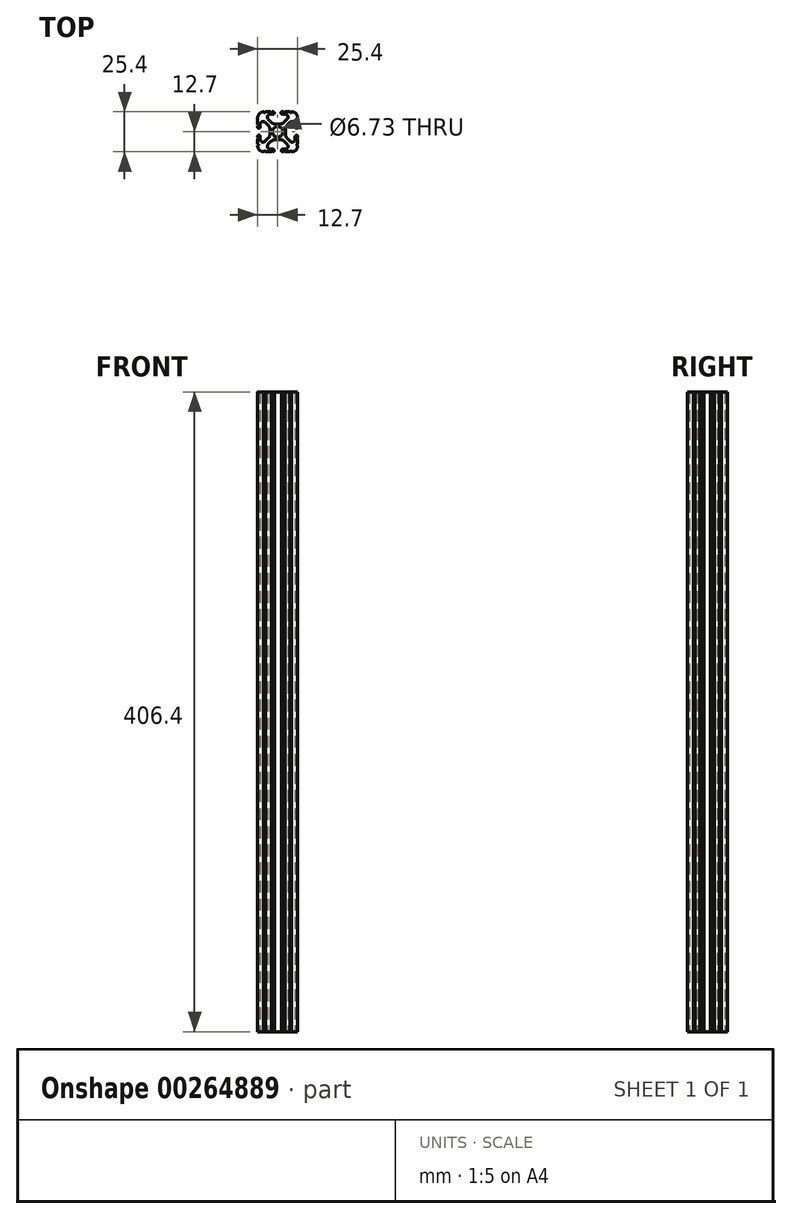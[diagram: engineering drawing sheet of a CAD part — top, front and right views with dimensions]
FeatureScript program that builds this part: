
annotation { "Feature Type Name" : "Feature", "Feature Type Description" : "" }
export const myFeature = defineFeature(function(context is Context, id is Id, definition is map)
    precondition{}
    {
        {
            var Q0;
            Q0=qCreatedBy(makeId("Top.planeOp"),FACE);
            var sketch = newSketch(context, id + "F0", { "sketchPlane" : qUnion([Q0])});
            skCircle(sketch, "E0", {"center": v(-12.7, 12.7) * mm, "radius": 3.36 * mm});
            skLineSegment(sketch, "E1.bottom", {"start": v(-11.24, 17.64) * mm, "end": v(-14.16, 17.64) * mm});
            skLineSegment(sketch, "E1.top", {"start": v(-11.24, 7.76) * mm, "end": v(-14.16, 7.76) * mm});
            skLineSegment(sketch, "E1.left", {"start": v(-7.76, 14.16) * mm, "end": v(-7.76, 11.24) * mm});
            skLineSegment(sketch, "E1.right", {"start": v(-17.64, 14.16) * mm, "end": v(-17.64, 11.24) * mm});
            skPoint(sketch, "E2.visualSharp", {"position": v(-25.4, 25.4) * mm});
            skPoint(sketch, "E3.visualSharp", {"position": v(0, 25.4) * mm});
            skPoint(sketch, "E4.visualSharp", {"position": v(0, 0) * mm});
            skPoint(sketch, "E5.visualSharp", {"position": v(-25.4, 0) * mm});
            skLineSegment(sketch, "E6.0", {"start": v(-18.7, 20.6) * mm, "end": v(-16.85, 18.76) * mm});
            skLineSegment(sketch, "E7.0", {"start": v(-20.6, 18.7) * mm, "end": v(-18.76, 16.85) * mm});
            skPoint(sketch, "E8.orphan", {"position": v(-23.85, 1.55) * mm});
            skPoint(sketch, "E9.orphan", {"position": v(-23.85, 23.85) * mm});
            skPoint(sketch, "E10.orphan", {"position": v(-1.55, 23.85) * mm});
            skPoint(sketch, "E11.orphan", {"position": v(-1.55, 1.55) * mm});
            skLineSegment(sketch, "E12", {"start": v(-8.55, 6.64) * mm, "end": v(-6.7, 4.8) * mm});
            skLineSegment(sketch, "E13.0", {"start": v(-18.7, 4.8) * mm, "end": v(-16.85, 6.64) * mm});
            skLineSegment(sketch, "E14.0", {"start": v(-20.6, 6.7) * mm, "end": v(-18.76, 8.55) * mm});
            skLineSegment(sketch, "E15.0", {"start": v(-8.55, 18.76) * mm, "end": v(-6.7, 20.6) * mm});
            skPoint(sketch, "E16.visualSharp", {"position": v(-23.85, 21.95) * mm});
            skArc(sketch, "E16.filletArc", {"start": v(-20.6, 18.7) * mm, "mid": v(-22.68, 19.1) * mm, "end": v(-23.85, 17.35) * mm});
            skPoint(sketch, "E17.visualSharp", {"position": v(-21.95, 23.85) * mm});
            skArc(sketch, "E17.filletArc", {"start": v(-17.35, 23.85) * mm, "mid": v(-19.1, 22.68) * mm, "end": v(-18.7, 20.6) * mm});
            skPoint(sketch, "E18.visualSharp", {"position": v(-5.34, 23.85) * mm});
            skLineSegment(sketch, "E19", {"start": v(-17.35, 23.85) * mm, "end": v(-15.58, 23.85) * mm});
            skLineSegment(sketch, "E20", {"start": v(-23.85, 17.35) * mm, "end": v(-23.85, 15.62) * mm});
            skLineSegment(sketch, "E21", {"start": v(-8.05, 1.55) * mm, "end": v(-9.78, 1.55) * mm});
            skArc(sketch, "E22.filletArc", {"start": v(-6.7, 20.6) * mm, "mid": v(-6.3, 22.68) * mm, "end": v(-8.05, 23.85) * mm});
            skPoint(sketch, "E23.visualSharp", {"position": v(-1.55, 3.45) * mm});
            skPoint(sketch, "E24.visualSharp", {"position": v(-3.45, 1.55) * mm});
            skArc(sketch, "E24.filletArc", {"start": v(-8.05, 1.55) * mm, "mid": v(-6.3, 2.73) * mm, "end": v(-6.7, 4.8) * mm});
            skArc(sketch, "E25.filletArc", {"start": v(-18.7, 4.8) * mm, "mid": v(-19.1, 2.73) * mm, "end": v(-17.35, 1.55) * mm});
            skArc(sketch, "E26.filletArc", {"start": v(-23.85, 8.05) * mm, "mid": v(-22.68, 6.3) * mm, "end": v(-20.6, 6.7) * mm});
            skLineSegment(sketch, "E27.bottom", {"start": v(-4.9, 0) * mm, "end": v(-8.05, 0) * mm});
            skLineSegment(sketch, "E27.top", {"start": v(-4.92, 25.4) * mm, "end": v(-8.05, 25.4) * mm});
            skLineSegment(sketch, "E27.left", {"start": v(0, 4.9) * mm, "end": v(0, 8.05) * mm});
            skLineSegment(sketch, "E27.right", {"start": v(-25.4, 4.9) * mm, "end": v(-25.4, 8.05) * mm});
            skArc(sketch, "E28.filletArc", {"start": v(-25.4, 3.81) * mm, "mid": v(-24.28, 1.12) * mm, "end": v(-21.59, 0) * mm});
            skArc(sketch, "E29.filletArc", {"start": v(-3.81, 0) * mm, "mid": v(-1.12, 1.12) * mm, "end": v(0, 3.8) * mm});
            skArc(sketch, "E30.filletArc", {"start": v(0, 21.59) * mm, "mid": v(-1.12, 24.28) * mm, "end": v(-3.8, 25.4) * mm});
            skArc(sketch, "E31.filletArc", {"start": v(-21.59, 25.4) * mm, "mid": v(-24.28, 24.28) * mm, "end": v(-25.4, 21.59) * mm});
            skPoint(sketch, "E32.newPointA", {"position": v(-17.64, 7.76) * mm});
            skArc(sketch, "E32.filletArc", {"start": v(-14.16, 7.76) * mm, "mid": v(-15.62, 7.47) * mm, "end": v(-16.85, 6.64) * mm});
            skPoint(sketch, "E33.newPointA", {"position": v(-7.76, 7.76) * mm});
            skArc(sketch, "E33.filletArc", {"start": v(-8.55, 6.64) * mm, "mid": v(-9.78, 7.47) * mm, "end": v(-11.24, 7.76) * mm});
            skArc(sketch, "E34.filletArc", {"start": v(-7.76, 11.24) * mm, "mid": v(-7.47, 9.78) * mm, "end": v(-6.64, 8.55) * mm});
            skArc(sketch, "E35.filletArc", {"start": v(-6.64, 16.85) * mm, "mid": v(-7.47, 15.62) * mm, "end": v(-7.76, 14.16) * mm});
            skPoint(sketch, "E36.newPointB", {"position": v(-7.76, 17.64) * mm});
            skArc(sketch, "E36.filletArc", {"start": v(-11.24, 17.64) * mm, "mid": v(-9.78, 17.93) * mm, "end": v(-8.55, 18.76) * mm});
            skPoint(sketch, "E37.newPointB", {"position": v(-17.64, 17.64) * mm});
            skArc(sketch, "E37.filletArc", {"start": v(-16.85, 18.76) * mm, "mid": v(-15.62, 17.93) * mm, "end": v(-14.16, 17.64) * mm});
            skArc(sketch, "E38.filletArc", {"start": v(-17.64, 14.16) * mm, "mid": v(-17.93, 15.62) * mm, "end": v(-18.76, 16.85) * mm});
            skArc(sketch, "E39.filletArc", {"start": v(-18.76, 8.55) * mm, "mid": v(-17.93, 9.78) * mm, "end": v(-17.64, 11.24) * mm});
            skLineSegment(sketch, "E40", {"start": v(-6.64, 8.55) * mm, "end": v(-4.8, 6.7) * mm});
            skPoint(sketch, "E41.visualSharp", {"position": v(-1.55, 21.95) * mm});
            skArc(sketch, "E42.filletArc", {"start": v(-4.8, 6.7) * mm, "mid": v(-2.73, 6.3) * mm, "end": v(-1.55, 8.05) * mm});
            skLineSegment(sketch, "E43", {"start": v(-1.55, 8.05) * mm, "end": v(-1.55, 9.78) * mm});
            skLineSegment(sketch, "E44", {"start": v(-6.64, 16.85) * mm, "end": v(-4.8, 18.7) * mm});
            skArc(sketch, "E45.filletArc", {"start": v(-1.55, 17.35) * mm, "mid": v(-2.73, 19.1) * mm, "end": v(-4.8, 18.7) * mm});
            skArc(sketch, "E46", {"start": v(-23.85, 9.78) * mm, "mid": v(-24.63, 10.56) * mm, "end": v(-25.4, 9.78) * mm});
            skArc(sketch, "E47", {"start": v(-25.4, 15.62) * mm, "mid": v(-24.63, 14.86) * mm, "end": v(-23.85, 15.62) * mm});
            skArc(sketch, "E48", {"start": v(-15.62, 23.85) * mm, "mid": v(-14.83, 24.63) * mm, "end": v(-15.62, 25.4) * mm});
            skArc(sketch, "E49", {"start": v(-9.78, 25.4) * mm, "mid": v(-10.6, 24.63) * mm, "end": v(-9.78, 23.85) * mm});
            skArc(sketch, "E50", {"start": v(-1.55, 15.62) * mm, "mid": v(-0.77, 14.88) * mm, "end": v(0, 15.62) * mm});
            skArc(sketch, "E51", {"start": v(0, 9.78) * mm, "mid": v(-0.77, 10.5) * mm, "end": v(-1.55, 9.78) * mm});
            skArc(sketch, "E52", {"start": v(-9.78, 1.55) * mm, "mid": v(-10.4, 0.77) * mm, "end": v(-9.78, 0) * mm});
            skArc(sketch, "E53", {"start": v(-15.62, 0) * mm, "mid": v(-14.85, 0.77) * mm, "end": v(-15.62, 1.55) * mm});
            skLineSegment(sketch, "E54.trimOffspring", {"start": v(-15.62, 1.55) * mm, "end": v(-17.35, 1.55) * mm});
            skLineSegment(sketch, "E55.trimOffspring", {"start": v(-16.7, 0) * mm, "end": v(-20.5, 0) * mm});
            skLineSegment(sketch, "E56.trimOffspring", {"start": v(-1.55, 15.62) * mm, "end": v(-1.55, 17.35) * mm});
            skLineSegment(sketch, "E57.trimOffspring", {"start": v(0, 15.62) * mm, "end": v(0, 16.26) * mm});
            skLineSegment(sketch, "E58.trimOffspring", {"start": v(-23.85, 9.78) * mm, "end": v(-23.85, 8.05) * mm});
            skLineSegment(sketch, "E59.trimOffspring", {"start": v(-25.4, 15.62) * mm, "end": v(-25.4, 16.26) * mm});
            skLineSegment(sketch, "E60.trimOffspring", {"start": v(-9.86, 23.85) * mm, "end": v(-8.05, 23.85) * mm});
            skLineSegment(sketch, "E61.trimOffspring", {"start": v(-15.58, 25.4) * mm, "end": v(-16.25, 25.4) * mm});
            skPoint(sketch, "E62.start.orphan", {"position": v(-15.62, 17.93) * mm});
            skPoint(sketch, "E63.start.orphan", {"position": v(-9.78, 17.93) * mm});
            skPoint(sketch, "E64.start.orphan", {"position": v(-7.47, 15.62) * mm});
            skPoint(sketch, "E65.start.orphan", {"position": v(-7.47, 9.78) * mm});
            skPoint(sketch, "E66.start.orphan", {"position": v(-17.93, 15.62) * mm});
            skPoint(sketch, "E67.start.orphan", {"position": v(-17.93, 9.78) * mm});
            skPoint(sketch, "E68.start.orphan", {"position": v(-9.78, 7.47) * mm});
            skPoint(sketch, "E69.start.orphan", {"position": v(-15.62, 7.47) * mm});
            skPoint(sketch, "E70.endSnap0", {"position": v(0, 18.6) * mm});
            skPoint(sketch, "E71.startSnap0", {"position": v(-1.55, 8.92) * mm});
            skArc(sketch, "E72", {"start": v(-4.92, 25.4) * mm, "mid": v(-4.37, 24.9) * mm, "end": v(-3.81, 25.4) * mm});
            skArc(sketch, "E73", {"start": v(-9.14, 25.4) * mm, "mid": v(-8.6, 24.86) * mm, "end": v(-8.05, 25.4) * mm});
            skArc(sketch, "E74", {"start": v(-17.35, 25.4) * mm, "mid": v(-16.8, 24.86) * mm, "end": v(-16.25, 25.4) * mm});
            skArc(sketch, "E75", {"start": v(-21.6, 25.4) * mm, "mid": v(-21.04, 24.85) * mm, "end": v(-20.49, 25.4) * mm});
            skLineSegment(sketch, "E76", {"start": v(-25.4, 21.59) * mm, "end": v(-25.4, 20.5) * mm});
            skArc(sketch, "E77", {"start": v(-25.4, 16.26) * mm, "mid": v(-24.84, 16.8) * mm, "end": v(-25.4, 17.35) * mm});
            skArc(sketch, "E78", {"start": v(-25.4, 8.05) * mm, "mid": v(-24.9, 8.6) * mm, "end": v(-25.4, 9.15) * mm});
            skArc(sketch, "E79", {"start": v(-25.4, 3.81) * mm, "mid": v(-24.85, 4.36) * mm, "end": v(-25.4, 4.9) * mm});
            skArc(sketch, "E80", {"start": v(-20.5, 0) * mm, "mid": v(-21.04, 0.55) * mm, "end": v(-21.59, 0) * mm});
            skArc(sketch, "E81", {"start": v(-15.62, 0) * mm, "mid": v(-16.16, 0.54) * mm, "end": v(-16.7, 0) * mm});
            skArc(sketch, "E82", {"start": v(-8.05, 0) * mm, "mid": v(-8.6, 0.55) * mm, "end": v(-9.15, 0) * mm});
            skArc(sketch, "E83", {"start": v(-3.81, 0) * mm, "mid": v(-4.35, 0.54) * mm, "end": v(-4.9, 0) * mm});
            skLineSegment(sketch, "E84.trimOffspring", {"start": v(-17.35, 25.4) * mm, "end": v(-20.49, 25.4) * mm});
            skLineSegment(sketch, "E85.trimOffspring", {"start": v(-25.4, 17.35) * mm, "end": v(-25.4, 21.59) * mm});
            skLineSegment(sketch, "E86.trimOffspring", {"start": v(-25.4, 9.15) * mm, "end": v(-25.4, 9.78) * mm});
            skLineSegment(sketch, "E87.trimOffspring", {"start": v(-9.15, 0) * mm, "end": v(-9.78, 0) * mm});
            skArc(sketch, "E88", {"start": v(0, 4.9) * mm, "mid": v(-0.54, 4.36) * mm, "end": v(0, 3.8) * mm});
            skArc(sketch, "E89", {"start": v(0, 9.15) * mm, "mid": v(-0.54, 8.6) * mm, "end": v(0, 8.05) * mm});
            skLineSegment(sketch, "E90.trimOffspring", {"start": v(0, 9.15) * mm, "end": v(0, 9.78) * mm});
            skArc(sketch, "E91", {"start": v(0, 21.59) * mm, "mid": v(-0.55, 21.04) * mm, "end": v(0, 20.5) * mm});
            skArc(sketch, "E92", {"start": v(0, 17.35) * mm, "mid": v(-0.55, 16.8) * mm, "end": v(0, 16.26) * mm});
            skLineSegment(sketch, "E93.trimOffspring", {"start": v(0, 17.35) * mm, "end": v(0, 20.5) * mm});
            skLineSegment(sketch, "E94.trimOffspring", {"start": v(-9.14, 25.4) * mm, "end": v(-9.86, 25.4) * mm});
            skSolve(sketch);
        }
        {
            var Q0;
            Q0=qSketchRegion(id+"F0",true);
            extrude(context, id + "F1", {"entities" : qUnion([Q0]), "depth" : 406.4 * mm});
        }
    });
